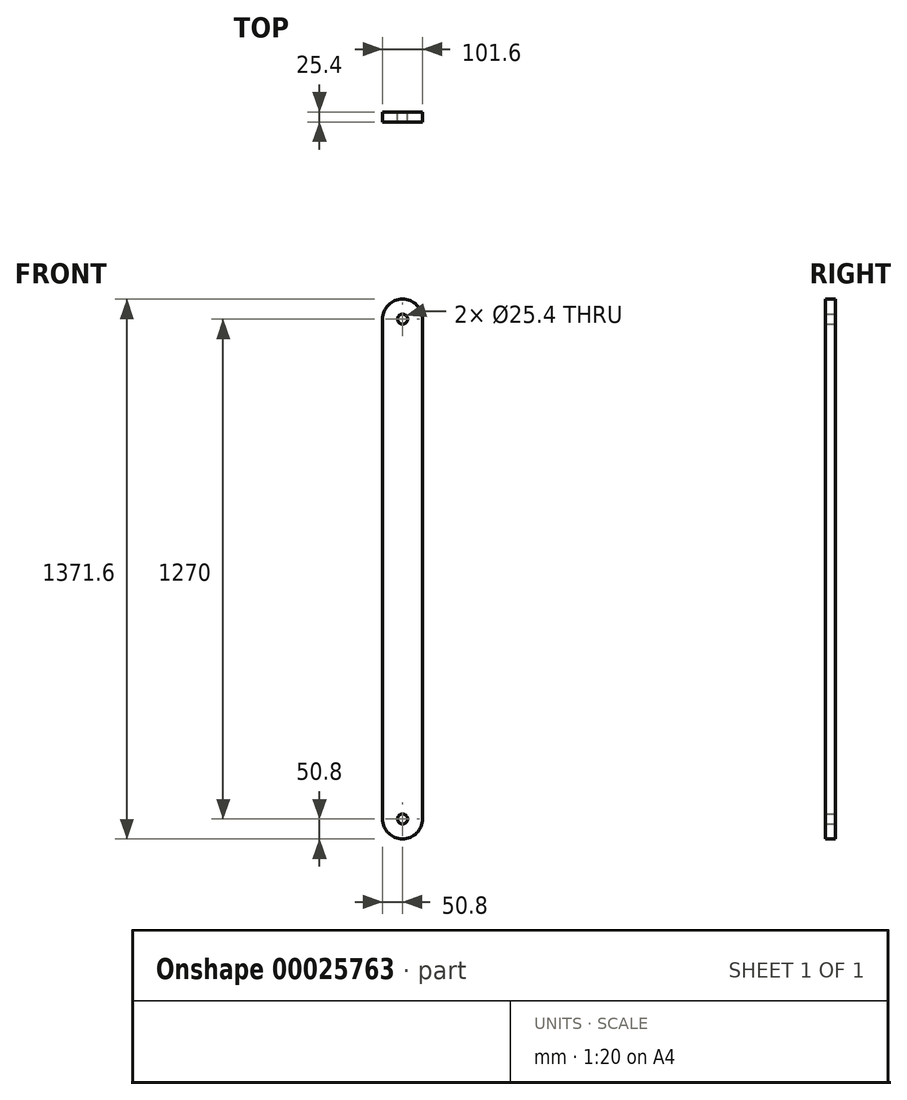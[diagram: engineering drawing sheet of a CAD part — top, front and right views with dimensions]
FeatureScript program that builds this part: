
annotation { "Feature Type Name" : "Feature", "Feature Type Description" : "" }
export const myFeature = defineFeature(function(context is Context, id is Id, definition is map)
    precondition{}
    {
        {
            var Q0;
            Q0=qCreatedBy(makeId("Front.planeOp"),FACE);
            var sketch = newSketch(context, id + "F0", { "sketchPlane" : qUnion([Q0])});
            skCircle(sketch, "E0", {"center": v(0, 0) * mm, "radius": 12.7 * mm});
            skLineSegment(sketch, "E1", {"start": v(50.8, 0) * mm, "end": v(50.8, 1270) * mm});
            skLineSegment(sketch, "E2", {"start": v(-50.8, 0) * mm, "end": v(-50.8, 1270) * mm});
            skArc(sketch, "E3", {"start": v(-50.8, 0) * mm, "mid": v(0, -50.8) * mm, "end": v(50.8, 0) * mm});
            skArc(sketch, "E4", {"start": v(50.8, 1270) * mm, "mid": v(0, 1320.8) * mm, "end": v(-50.8, 1270) * mm});
            skCircle(sketch, "E5", {"center": v(0, 1270) * mm, "radius": 12.7 * mm});
            skSolve(sketch);
        }
        {
            var Q0;
            Q0=qSketchRegion(id+"F0",true);
            extrude(context, id + "F1", {"entities" : qUnion([Q0]), "depth" : 25.4 * mm});
        }
    });
